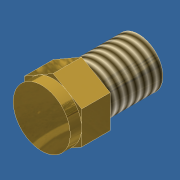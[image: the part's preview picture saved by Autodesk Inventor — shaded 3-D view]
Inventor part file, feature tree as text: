
AUTODESK INVENTOR PART (.ipt)
format: ipt  version: unknown  size: 191,488 bytes
history: native  units: in
note: dims shown in document units (in); Inventor stores cm internally (conversion verified against a paired STEP export)
features: extrude x3, sketch x3, thread x1
ambient origin geometry x8: Origin, YZ Plane, XZ Plane, XY Plane, X Axis, Y Axis, Z Axis, Center Point
bodies: Solid1 (feature_tree)
feature tree (7):
  extrude  "Extrusion1"  Depth=0.5in TaperAngle=0.0deg
  thread  "Thread1"  [1 undecoded]
  extrude  "Extrusion2"  TaperAngle=0.0deg  [1 undecoded]
  extrude  "Extrusion3"  Depth=0.1in TaperAngle=0.0deg
  sketch  "Sketch1"  dims[d0=0.425in d1=0.5in d2=0.0in d3=1.0in d4=0.0in]
  sketch  "Sketch2"  dims[d5=0.5in d6=0.0in]
  sketch  "Sketch3"  dims[d7=0.25in d8=0.0in d9=0.1in d10=0.0in]
note: 2 required parameter values undecoded (feature->parameter linkage not recoverable at this tier; creation-order binding heuristic only, values carry confidence <= 0.55)
